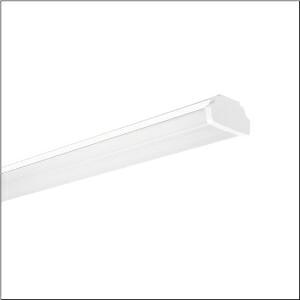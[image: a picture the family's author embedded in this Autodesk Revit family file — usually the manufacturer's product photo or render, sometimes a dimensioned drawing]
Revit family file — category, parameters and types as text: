
# Revit family: modario_r__31_ho_53bm812m1v4120_c9f3
name_source: partatom
category: Lighting Fixtures
units: mm (PartAtom-declared; Revit-internal decimal feet)

## family parameters
Cut with Voids When Loaded = No
Host = Face
Light Source = No
Part Type = Normal
Room Calculation Point = No
Round Connector Dimension = Use Diameter
Shared = No

## types (1)
- --- (1 x LED, 12380 lm, 77.3 W, 4000K)
    Apparent Load = 77 VA
    CIE Flux Codes = 47 80 95 92 100
    Color Rendering = 80
    Color Temperature = 4000K
    Default Elevation = 1800 mm
    Description = Modario® 31 HO, luminaire insert, of sheet steel, coil coated, white, length: 1.495mm, width: 81mm, height: 82mm, 5x system unit, system units: 299mm, LED rated luminous flux: 12.380lm, light colour: 840, control gear: ON/OFF Multilumen, control gear: ECG Multilumen, with plug, 3-pole, with phase selection, mains connection: 220..240V, AC, 50/60Hz, rated input power: 77W, through-wiring accessed according to module size, primary optical cover: cover, of PMMA, light emission: direct distribution, primary light characteristic: symmetric, protection rating (complete): IP20, protection rating (LED compartment): IP50, insulation class (complete): insulation class I (protective earthing), certification: CE, ENEC, VDE, UKCA, impact resistance: IK03, permissible ambient temperature for indoor applications: -35..+35°C, corresponds to IFS (International Featured Standards) requirements for safety and quality in the food industry, reducing of maximum allowable ambient temperature of 5°C with ceiling mounting, packaging unit: 1 piece
    Height = 92 mm
    Lamp = 1 x LED
    Lamp Light Flux = 12380 lm
    Lamp Power = 77.3 W
    Lamp count = 1
    Length = 1495 mm
    Luminous efficacy = 160 lm/W
    Manufacturer = Siteco
    ModVariant = No
    Model = 53BM812M1V4120
    Mounting Place = Ceiling
    Mounting Type = Pendant
    Number of Poles = 1
    OnlyDefault = Yes
    Power Factor = 1
    Product Name = Modario® 31 HO
    Product group = luminaire insert
    ProductGroupID = 901
    Protection Class = Protection class I
    Protection Degree = IP 20
    RLX_Detail_Level = 1
    RLX_Emergency_Light_Flux = 0 lm
    RLX_Emergency_Type = 0
    RLX_Emergency_Type_DB = No
    RlxData = <blob elided: 40009 chars, md5=9943aace>
    Socket = socket
    Standby Power = 0 W
    System Light Flux = 12380 lm
    System Power = 77 W
    Type Comments = factory setting: luminous flux: 100 % | (A | C | E) | 173 mA
    Type Image = l_1300283.jpg
    URL = http://relux.com
    VarID = @adj_140287
    Voltage = 0 V
    Weight = 0.00 kg
    Width = 81 mm

## geometry (parser evidence)
native form markers: Blend x4, Sweep x11
no freeform markers — native parametric forms only
